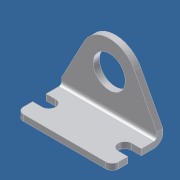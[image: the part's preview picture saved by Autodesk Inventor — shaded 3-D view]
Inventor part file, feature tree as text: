
AUTODESK INVENTOR PART (.ipt)
format: ipt  version: 2012 (Build 160160000, 160)  size: 154,112 bytes
history: native  units: in
note: dims shown in document units (in); Inventor stores cm internally (conversion verified against a paired STEP export)
features: other x126, extrude x7, sketch x7
ambient origin geometry x8: Origin, YZ Plane, XZ Plane, XY Plane, X Axis, Y Axis, Z Axis, Center Point
bodies: Solid1 (feature_tree)
feature tree (140):
  extrude  "Extrusion1"  Depth=0.18in TaperAngle=0.0deg
  extrude  "Extrusion2"  Depth=0.18in TaperAngle=0.0deg
  extrude  "Extrusion3"  Depth=0.18in TaperAngle=0.0deg
  extrude  "Extrusion4"  [1 undecoded]
  extrude  "Extrusion5"  [1 undecoded]
  extrude  "Extrusion6"  [1 undecoded]
  extrude  "Extrusion7"  [1 undecoded]
  other  "h1_XY"
  other  "h1_YZ"
  other  "h1_ZX"
  other  "h1_X"
  other  "h1_Y"
  other  "h1_Z"
  other  "h1_Center"
  other  "d1_XY"
  other  "d1_YZ"
  other  "d1_ZX"
  other  "d1_X"
  other  "d1_Y"
  other  "d1_Z"
  other  "d1_Center"
  other  "h2_XY"
  other  "h2_YZ"
  other  "h2_ZX"
  other  "h2_X"
  other  "h2_Y"
  other  "h2_Z"
  other  "h2_Center"
  other  "d2_XY"
  other  "d2_YZ"
  other  "d2_ZX"
  other  "d2_X"
  other  "d2_Y"
  other  "d2_Z"
  other  "d2_Center"
  other  "h3_XY"
  other  "h3_YZ"
  other  "h3_ZX"
  other  "h3_X"
  other  "h3_Y"
  other  "h3_Z"
  other  "h3_Center"
  other  "h4_XY"
  other  "h4_YZ"
  other  "h4_ZX"
  other  "h4_X"
  other  "h4_Y"
  other  "h4_Z"
  other  "h4_Center"
  other  "h5_XY"
  other  "h5_YZ"
  other  "h5_ZX"
  other  "h5_X"
  other  "h5_Y"
  other  "h5_Z"
  other  "h5_Center"
  other  "h6_XY"
  other  "h6_YZ"
  other  "h6_ZX"
  other  "h6_X"
  other  "h6_Y"
  other  "h6_Z"
  other  "h6_Center"
  other  "l1_XY"
  other  "l1_YZ"
  other  "l1_ZX"
  other  "l1_X"
  other  "l1_Y"
  other  "l1_Z"
  other  "l1_Center"
  other  "l2_XY"
  other  "l2_YZ"
  other  "l2_ZX"
  other  "l2_X"
  other  "l2_Y"
  other  "l2_Z"
  other  "l2_Center"
  other  "l3_XY"
  other  "l3_YZ"
  other  "l3_ZX"
  other  "l3_X"
  other  "l3_Y"
  other  "l3_Z"
  other  "l3_Center"
  other  "l4_XY"
  other  "l4_YZ"
  other  "l4_ZX"
  other  "l4_X"
  other  "l4_Y"
  other  "l4_Z"
  other  "l4_Center"
  other  "l5_XY"
  other  "l5_YZ"
  other  "l5_ZX"
  other  "l5_X"
  other  "l5_Y"
  other  "l5_Z"
  other  "l5_Center"
  other  "l6_XY"
  other  "l6_YZ"
  other  "l6_ZX"
  other  "l6_X"
  other  "l6_Y"
  other  "l6_Z"
  other  "l6_Center"
  other  "l7_XY"
  other  "l7_YZ"
  other  "l7_ZX"
  other  "l7_X"
  other  "l7_Y"
  other  "l7_Z"
  other  "l7_Center"
  other  "l8_XY"
  other  "l8_YZ"
  other  "l8_ZX"
  other  "l8_X"
  other  "l8_Y"
  other  "l8_Z"
  other  "l8_Center"
  other  "mounting_bracket_XY"
  other  "mounting_bracket_YZ"
  other  "mounting_bracket_ZX"
  other  "mounting_bracket_X"
  other  "mounting_bracket_Y"
  other  "mounting_bracket_Z"
  other  "mounting_bracket_Center"
  other  "mounting_bracket_1_XY"
  other  "mounting_bracket_1_YZ"
  other  "mounting_bracket_1_ZX"
  other  "mounting_bracket_1_X"
  other  "mounting_bracket_1_Y"
  other  "mounting_bracket_1_Z"
  other  "mounting_bracket_1_Center"
  sketch  "Sketch_1"  dims[d0=1.875in d1=0.0in d2=0.18in d3=0.0in]
  sketch  "Sketch_2"  dims[d4=0.18in d5=0.0in d6=0.18in d7=0.0in]
  sketch  "Sketch_3"  dims[d8=0.18in d9=0.0in d10=0.18in d11=0.0in]
  sketch  "Sketch_6"  dims[d12=0.18in d13=0.0in]
  sketch  "Sketch_7"
  sketch  "Sketch_8"
  sketch  "Sketch_9"
note: 4 required parameter values undecoded (feature->parameter linkage not recoverable at this tier; creation-order binding heuristic only, values carry confidence <= 0.55)
